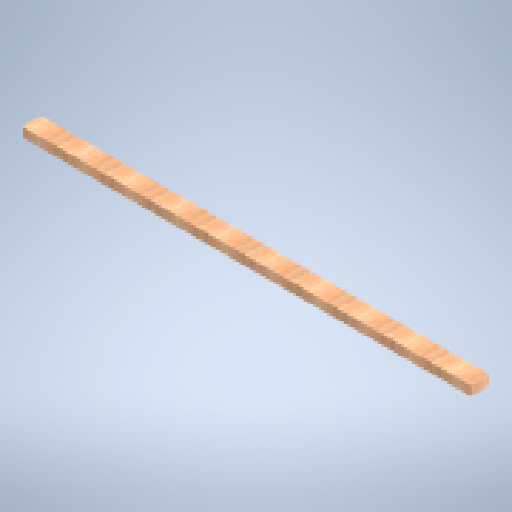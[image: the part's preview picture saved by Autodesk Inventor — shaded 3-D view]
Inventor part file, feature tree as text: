
AUTODESK INVENTOR PART (.ipt)
format: ipt  version: 2025 (Build 290162000, 162)  size: 295,936 bytes
history: native  units: in
note: dims shown in document units (in); Inventor stores cm internally (conversion verified against a paired STEP export)
features: extrude x1, move_body x1, sketch x1
ambient origin geometry x8: Origin, YZ Plane, XZ Plane, XY Plane, X Axis, Y Axis, Z Axis, Center Point
bodies: Solid1 (feature_tree)
feature tree (3):
  extrude  "Extrusion1"  Depth=4.0in
  move_body  "Move Body1"
  sketch  "Sketch1"  dims[d0=96.0in d1=4.0in d2=2.0in d3=0.0in d6=90.0deg]
